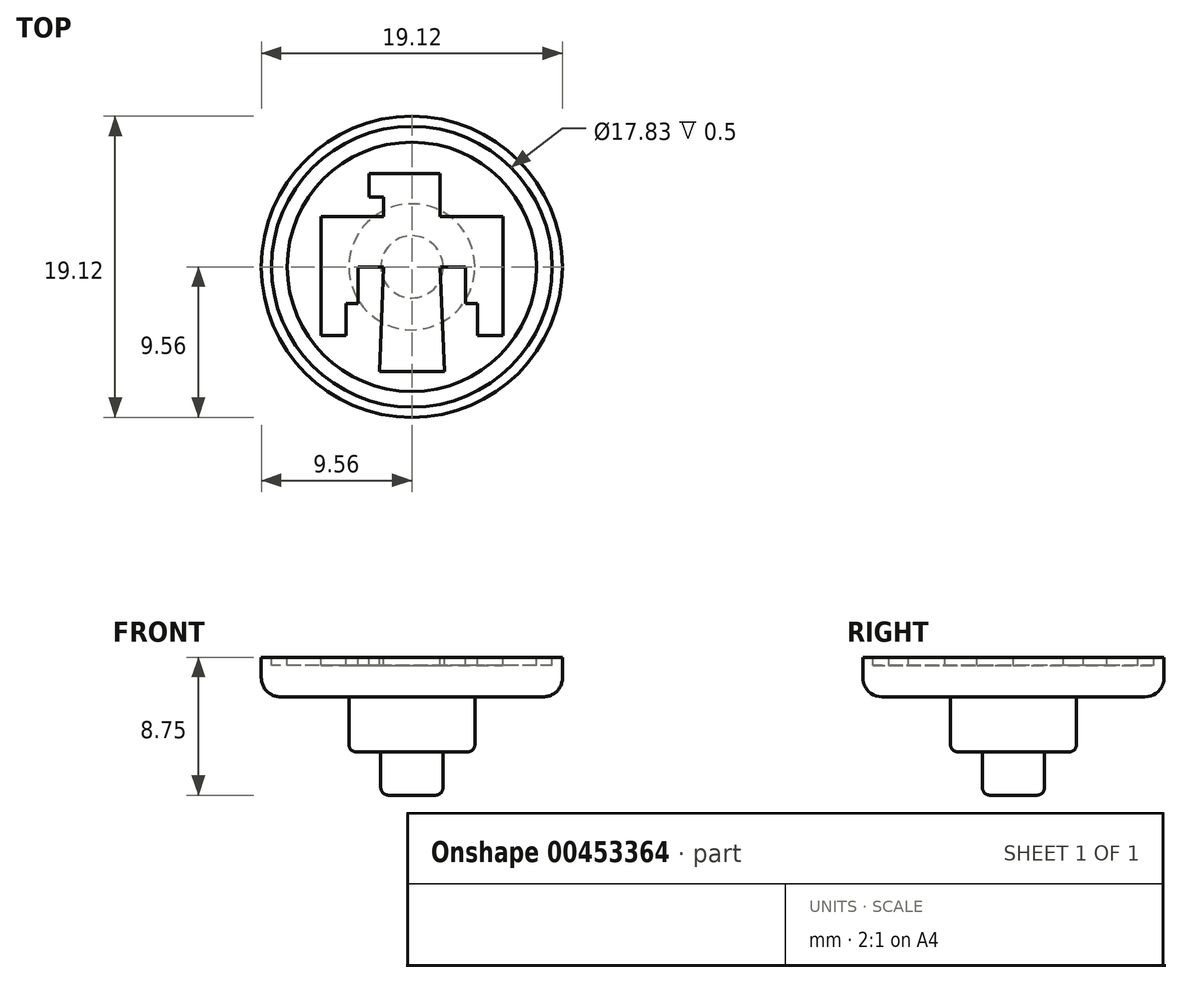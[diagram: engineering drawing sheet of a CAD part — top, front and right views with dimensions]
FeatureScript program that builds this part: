
annotation { "Feature Type Name" : "Feature", "Feature Type Description" : "" }
export const myFeature = defineFeature(function(context is Context, id is Id, definition is map)
    precondition{}
    {
        {
            var Q0;
            Q0=qCreatedBy(makeId("Top.planeOp"),FACE);
            var sketch = newSketch(context, id + "F0", { "sketchPlane" : qUnion([Q0])});
            skCircle(sketch, "E0", {"center": v(0, 0) * mm, "radius": 9.56 * mm});
            skSolve(sketch);
        }
        {
            var Q0;
            Q0=makeQuery(id+"F0.imprint","IMPRINT",FACE,{"disambiguationData":[TD([[makeQuery(id+"F0.imprint","IMPRINT",EDGE,{"derivedFrom":sQuery(id+"F0.wireOp",EDGE,"E0")}),1.0]])]});
            extrude(context, id + "F1", {"entities" : qUnion([Q0]), "depth" : 2.5 * mm, "offsetDistance" : 25 * mm});
        }
        {
            var Q0;
            Q0=makeQuery(id+"F1.opExtrude","CAP_FACE",FACE,{"disambiguationData":[OSD([sQuery(id+"F0.wireOp",EDGE,"E0")])],"isStart":false});
            var sketch = newSketch(context, id + "F2", { "sketchPlane" : qUnion([Q0])});
            skLineSegment(sketch, "E1", {"start": v(-2.7, 5.93) * mm, "end": v(1.8, 5.93) * mm});
            skLineSegment(sketch, "E2", {"start": v(1.8, 5.93) * mm, "end": v(1.8, 3.18) * mm});
            skLineSegment(sketch, "E3", {"start": v(1.8, 3.18) * mm, "end": v(5.78, 3.18) * mm});
            skLineSegment(sketch, "E4", {"start": v(5.78, 3.18) * mm, "end": v(5.78, -4.35) * mm});
            skLineSegment(sketch, "E5", {"start": v(5.78, -4.35) * mm, "end": v(4.17, -4.35) * mm});
            skLineSegment(sketch, "E6", {"start": v(4.17, -4.35) * mm, "end": v(4.17, -2.32) * mm});
            skLineSegment(sketch, "E7", {"start": v(4.17, -2.32) * mm, "end": v(3.41, -2.32) * mm});
            skLineSegment(sketch, "E8", {"start": v(3.41, -2.32) * mm, "end": v(3.41, 0) * mm});
            skLineSegment(sketch, "E9", {"start": v(3.41, 0) * mm, "end": v(1.8, 0) * mm});
            skLineSegment(sketch, "E10", {"start": v(2.06, -6.66) * mm, "end": v(0, -6.66) * mm});
            skLineSegment(sketch, "E11", {"start": v(-2.7, 5.93) * mm, "end": v(-2.7, 4.43) * mm});
            skLineSegment(sketch, "E12", {"start": v(-2.7, 4.43) * mm, "end": v(-1.8, 4.43) * mm});
            skLineSegment(sketch, "E13.MirrorCS", {"start": v(-1.8, 3.18) * mm, "end": v(-5.78, 3.18) * mm});
            skLineSegment(sketch, "E14.MirrorCS", {"start": v(-5.78, 3.18) * mm, "end": v(-5.78, -4.35) * mm});
            skLineSegment(sketch, "E15.MirrorCS", {"start": v(-4.17, -4.35) * mm, "end": v(-4.17, -2.32) * mm});
            skLineSegment(sketch, "E16.MirrorCS", {"start": v(-4.17, -2.32) * mm, "end": v(-3.41, -2.32) * mm});
            skLineSegment(sketch, "E17.MirrorCS", {"start": v(-3.41, -2.32) * mm, "end": v(-3.41, 0) * mm});
            skLineSegment(sketch, "E18.MirrorCS", {"start": v(-3.41, 0) * mm, "end": v(-1.8, 0) * mm});
            skLineSegment(sketch, "E19.MirrorCS", {"start": v(-5.78, -4.35) * mm, "end": v(-4.17, -4.35) * mm});
            skLineSegment(sketch, "E20.MirrorCS", {"start": v(-2.06, -6.66) * mm, "end": v(0, -6.66) * mm});
            skLineSegment(sketch, "E21", {"start": v(-1.8, 4.43) * mm, "end": v(-1.8, 3.18) * mm});
            skCircle(sketch, "E22", {"center": v(0, 0) * mm, "radius": 7.92 * mm});
            skCircle(sketch, "E23", {"center": v(0, 0) * mm, "radius": 8.92 * mm});
            skLineSegment(sketch, "E24", {"start": v(-2.06, -6.66) * mm, "end": v(-1.8, 0) * mm});
            skLineSegment(sketch, "E25", {"start": v(2.06, -6.66) * mm, "end": v(1.8, 0) * mm});
            skSolve(sketch);
        }
        {
            var Q0;
            Q0=makeQuery(id+"F2.imprint","IMPRINT",FACE,{"disambiguationData":[TD([[makeQuery(id+"F2.imprint","IMPRINT",EDGE,{"derivedFrom":sQuery(id+"F2.wireOp",EDGE,"E1")}),-1.0]])]});
            var Q1;
            Q1=makeQuery(id+"F2.imprint","IMPRINT",FACE,{"disambiguationData":[TD([[makeQuery(id+"F2.imprint","IMPRINT",EDGE,{"derivedFrom":sQuery(id+"F2.wireOp",EDGE,"E22")}),-1.0]])]});
            extrude(context, id + "F3", {"entities" : qUnion([Q0, Q1]), "operationType" : NewBodyOperationType.REMOVE, "oppositeDirection" : true, "depth" : .5 * mm, "offsetDistance" : 25 * mm});
        }
        {
            var Q0;
            Q0=makeQuery(id+"F1.opExtrude","CAP_FACE",FACE,{"disambiguationData":[OSD([sQuery(id+"F0.wireOp",EDGE,"E0")])],"isStart":true});
            var sketch = newSketch(context, id + "F4", { "sketchPlane" : qUnion([Q0])});
            skCircle(sketch, "E26", {"center": v(0, 0) * mm, "radius": 4 * mm});
            skSolve(sketch);
        }
        {
            var Q0;
            Q0=makeQuery(id+"F4.imprint","IMPRINT",FACE,{"disambiguationData":[TD([[makeQuery(id+"F4.imprint","IMPRINT",EDGE,{"derivedFrom":sQuery(id+"F4.wireOp",EDGE,"E26")}),1.0]])]});
            extrude(context, id + "F5", {"entities" : qUnion([Q0]), "operationType" : NewBodyOperationType.ADD, "depth" : 3.5 * mm, "offsetDistance" : 25 * mm});
        }
        {
            var Q0;
            Q0=makeQuery(id+"F1.opExtrude","CAP_EDGE",EDGE,{"disambiguationData":[OSD([sQuery(id+"F0.wireOp",EDGE,"E0")])],"isStart":true});
            fillet(context, id + "F6", {"entities" : qUnion([Q0]), "radius" : 1.2 * mm, "tangentPropagation" : true, "allowEdgeOverflow" : false});
        }
        {
            var Q0;
            Q0=makeQuery(id+"F5.opExtrude","CAP_FACE",FACE,{"disambiguationData":[OSD([sQuery(id+"F4.wireOp",EDGE,"E26")])],"isStart":false});
            var sketch = newSketch(context, id + "F7", { "sketchPlane" : qUnion([Q0])});
            skCircle(sketch, "E27", {"center": v(0, 0) * mm, "radius": 1.98 * mm});
            skSolve(sketch);
        }
        {
            var Q0;
            Q0=makeQuery(id+"F7.imprint","IMPRINT",FACE,{"disambiguationData":[TD([[makeQuery(id+"F7.imprint","IMPRINT",EDGE,{"derivedFrom":sQuery(id+"F7.wireOp",EDGE,"E27")}),1.0]])]});
            extrude(context, id + "F8", {"entities" : qUnion([Q0]), "operationType" : NewBodyOperationType.ADD, "depth" : 2.75 * mm, "offsetDistance" : 25 * mm});
        }
        {
            var Q0;
            Q0=makeQuery(id+"F8.opExtrude","CAP_EDGE",EDGE,{"disambiguationData":[OSD([sQuery(id+"F7.wireOp",EDGE,"E27")])],"isStart":false});
            fillet(context, id + "F9", {"entities" : qUnion([Q0]), "radius" : 0.48 * mm, "tangentPropagation" : true, "allowEdgeOverflow" : false});
        }
        {
            var Q0;
            Q0=makeQuery(id+"F5.opExtrude","CAP_EDGE",EDGE,{"disambiguationData":[OSD([sQuery(id+"F4.wireOp",EDGE,"E26")])],"isStart":false});
            fillet(context, id + "F10", {"entities" : qUnion([Q0]), "radius" : 0.46 * mm, "tangentPropagation" : true, "allowEdgeOverflow" : false});
        }
    });
